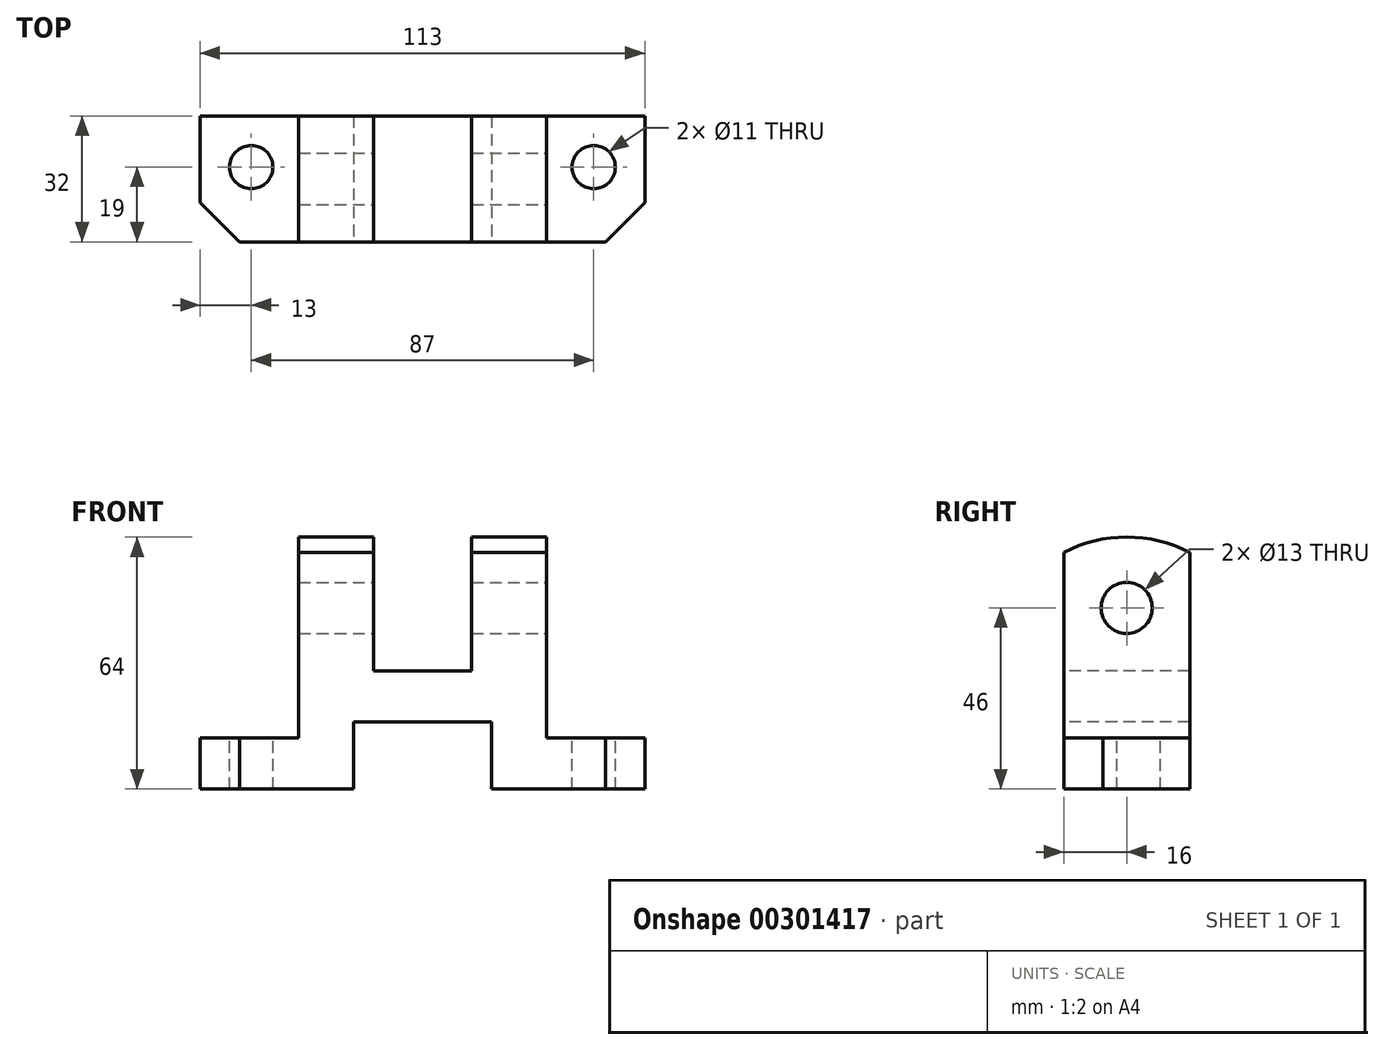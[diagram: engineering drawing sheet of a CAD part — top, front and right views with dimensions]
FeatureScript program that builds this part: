
annotation { "Feature Type Name" : "Feature", "Feature Type Description" : "" }
export const myFeature = defineFeature(function(context is Context, id is Id, definition is map)
    precondition{}
    {
        {
            var Q0;
            Q0=qCreatedBy(makeId("Front.planeOp"),FACE);
            var sketch = newSketch(context, id + "F0", { "sketchPlane" : qUnion([Q0])});
            skLineSegment(sketch, "E0.bottom", {"start": v(-56.5, 64) * mm, "end": v(56.5, 64) * mm});
            skLineSegment(sketch, "E0.top", {"start": v(-56.5, 0) * mm, "end": v(56.5, 0) * mm});
            skLineSegment(sketch, "E0.left", {"start": v(-56.5, 64) * mm, "end": v(-56.5, 0) * mm});
            skLineSegment(sketch, "E0.right", {"start": v(56.5, 64) * mm, "end": v(56.5, 0) * mm});
            skSolve(sketch);
        }
        {
            var Q0;
            Q0=makeQuery(id+"F0.imprint","IMPRINT",FACE,{"disambiguationData":[TD([[makeQuery(id+"F0.imprint","IMPRINT",EDGE,{"derivedFrom":sQuery(id+"F0.wireOp",EDGE,"E0.bottom")}),-1.0]])]});
            extrude(context, id + "F1", {"entities" : qUnion([Q0]), "endBound" : BoundingType.SYMMETRIC, "depth" : 32 * mm});
        }
        {
            var Q0;
            Q0=makeQuery(id+"F1.opExtrude","CAP_FACE",FACE,{"disambiguationData":[OSD([sQuery(id+"F0.wireOp",EDGE,"E0.bottom"),sQuery(id+"F0.wireOp",EDGE,"E0.top"),sQuery(id+"F0.wireOp",EDGE,"E0.left"),sQuery(id+"F0.wireOp",EDGE,"E0.right")])],"isStart":false});
            var sketch = newSketch(context, id + "F2", { "sketchPlane" : qUnion([Q0])});
            skLineSegment(sketch, "E1.bottom", {"start": v(31.5, 64) * mm, "end": v(56.5, 64) * mm});
            skLineSegment(sketch, "E1.top", {"start": v(31.5, 13) * mm, "end": v(56.5, 13) * mm});
            skLineSegment(sketch, "E1.left", {"start": v(31.5, 64) * mm, "end": v(31.5, 13) * mm});
            skLineSegment(sketch, "E1.right", {"start": v(56.5, 64) * mm, "end": v(56.5, 13) * mm});
            skLineSegment(sketch, "E2.bottom", {"start": v(-56.5, 64) * mm, "end": v(-31.5, 64) * mm});
            skLineSegment(sketch, "E2.top", {"start": v(-56.5, 13) * mm, "end": v(-31.5, 13) * mm});
            skLineSegment(sketch, "E2.left", {"start": v(-56.5, 64) * mm, "end": v(-56.5, 13) * mm});
            skLineSegment(sketch, "E2.right", {"start": v(-31.5, 64) * mm, "end": v(-31.5, 13) * mm});
            skLineSegment(sketch, "E3.bottom", {"start": v(-12.5, 64) * mm, "end": v(12.5, 64) * mm});
            skLineSegment(sketch, "E3.top", {"start": v(-12.5, 30) * mm, "end": v(12.5, 30) * mm});
            skLineSegment(sketch, "E3.left", {"start": v(-12.5, 64) * mm, "end": v(-12.5, 30) * mm});
            skLineSegment(sketch, "E3.right", {"start": v(12.5, 64) * mm, "end": v(12.5, 30) * mm});
            skLineSegment(sketch, "E4.bottom", {"start": v(-17.5, 17) * mm, "end": v(17.5, 17) * mm});
            skLineSegment(sketch, "E4.top", {"start": v(-17.5, 0) * mm, "end": v(17.5, 0) * mm});
            skLineSegment(sketch, "E4.left", {"start": v(-17.5, 17) * mm, "end": v(-17.5, 0) * mm});
            skLineSegment(sketch, "E4.right", {"start": v(17.5, 17) * mm, "end": v(17.5, 0) * mm});
            skSolve(sketch);
        }
        {
            var Q0;
            Q0=makeQuery(id+"F2.imprint","IMPRINT",FACE,{"disambiguationData":[TD([[makeQuery(id+"F2.imprint","IMPRINT",EDGE,{"derivedFrom":sQuery(id+"F2.wireOp",EDGE,"E2.bottom")}),-1.0]])]});
            var Q1;
            Q1=makeQuery(id+"F2.imprint","IMPRINT",FACE,{"disambiguationData":[TD([[makeQuery(id+"F2.imprint","IMPRINT",EDGE,{"derivedFrom":sQuery(id+"F2.wireOp",EDGE,"E1.bottom")}),-1.0]])]});
            var Q2;
            Q2=makeQuery(id+"F2.imprint","IMPRINT",FACE,{"disambiguationData":[TD([[makeQuery(id+"F2.imprint","IMPRINT",EDGE,{"derivedFrom":sQuery(id+"F2.wireOp",EDGE,"E3.bottom")}),-1.0]])]});
            var Q3;
            Q3=makeQuery(id+"F2.imprint","IMPRINT",FACE,{"disambiguationData":[TD([[makeQuery(id+"F2.imprint","IMPRINT",EDGE,{"derivedFrom":sQuery(id+"F2.wireOp",EDGE,"E4.bottom")}),-1.0]])]});
            extrude(context, id + "F3", {"entities" : qUnion([Q0, Q1, Q2, Q3]), "operationType" : NewBodyOperationType.REMOVE, "endBound" : BoundingType.THROUGH_ALL, "oppositeDirection" : true, "depth" : 25 * mm});
        }
        {
            var Q0;
            Q0=makeQuery(id+"F3.boolean.opBoolean","COPY",FACE,{"derivedFrom":makeQuery(id+"F3.opExtrude","SWEPT_FACE",FACE,{"disambiguationData":[OSD([sQuery(id+"F2.wireOp",EDGE,"E1.left")])]})});
            var sketch = newSketch(context, id + "F4", { "sketchPlane" : qUnion([Q0])});
            skArc(sketch, "E5", {"start": v(16, 60.13) * mm, "mid": v(0, 64) * mm, "end": v(-16, 60.13) * mm});
            skLineSegment(sketch, "E6", {"start": v(0, 0) * mm, "end": v(0, 85.12) * mm, "construction": true});
            skCircle(sketch, "E7", {"center": v(0, 46) * mm, "radius": 6.5 * mm});
            skSolve(sketch);
        }
        {
            var Q0;
            {var subQ0=sQuery(id+"F4.wireOp",EDGE,"E5");var subQ1=sQuery(id+"F2.wireOp",EDGE,"E1.left");var subQ2=makeQuery(id+"F3.boolean.opBoolean","COPY",EDGE,{"derivedFrom":makeQuery(id+"F3.opExtrude","CAP_EDGE",EDGE,{"disambiguationData":[OSD([subQ1])],"isStart":true})});var subQ3=makeQuery(id+"F4.imprint","INTERSECT",VERTEX,{"derivedFrom":[subQ2,subQ0]});Q0=makeQuery(id+"F4.imprint","IMPRINT",FACE,{"disambiguationData":[TD([[makeQuery(id+"F4.imprint","IMPRINT",EDGE,{"disambiguationData":[TD([[subQ3,1.0]])],"derivedFrom":subQ0}),-1.0]])]});}
            var Q1;
            {var subQ0=sQuery(id+"F4.wireOp",EDGE,"E5");var subQ1=sQuery(id+"F2.wireOp",EDGE,"E1.left");var subQ2=sQuery(id+"F0.wireOp",EDGE,"E0.bottom");var subQ5=makeQuery(id+"F3.boolean.opBoolean","COPY",EDGE,{"derivedFrom":makeQuery(id+"F3.opExtrude","SWEPT_EDGE",EDGE,{"disambiguationData":[OSD([subQ2,sQuery(id+"F2.wireOp",EDGE,"E1.bottom"),subQ1])]})});var subQ6=makeQuery(id+"F4.imprint","INTERSECT",VERTEX,{"derivedFrom":[subQ5,subQ0]});Q1=makeQuery(id+"F4.imprint","IMPRINT",FACE,{"disambiguationData":[TD([[makeQuery(id+"F4.imprint","IMPRINT",EDGE,{"disambiguationData":[TD([[subQ6,1.0]])],"derivedFrom":subQ0}),-1.0]])]});}
            var Q2;
            Q2=makeQuery(id+"F4.imprint","IMPRINT",FACE,{"disambiguationData":[TD([[makeQuery(id+"F4.imprint","IMPRINT",EDGE,{"derivedFrom":sQuery(id+"F4.wireOp",EDGE,"E7")}),1.0]])]});
            extrude(context, id + "F5", {"entities" : qUnion([Q0, Q1, Q2]), "operationType" : NewBodyOperationType.REMOVE, "endBound" : BoundingType.THROUGH_ALL, "oppositeDirection" : true, "depth" : 25 * mm});
        }
        {
            var Q0;
            Q0=qCreatedBy(makeId("Top.planeOp"),FACE);
            cPlane(context, id + "F6", {"entities" : qUnion([Q0]), "cplaneType" : CPlaneType.OFFSET, "offset" : 64 * mm, "width" : 150 * mm, "height" : 150 * mm});
        }
        {
            var Q0;
            Q0=qCreatedBy(id+"F6.planeOp",FACE);
            var sketch = newSketch(context, id + "F7", { "sketchPlane" : qUnion([Q0])});
            skCircle(sketch, "E8", {"center": v(43.5, 3) * mm, "radius": 5.5 * mm});
            skCircle(sketch, "E9", {"center": v(-43.5, 3) * mm, "radius": 5.5 * mm});
            skSolve(sketch);
        }
        {
            var Q0;
            Q0=makeQuery(id+"F7.imprint","IMPRINT",FACE,{"disambiguationData":[TD([[makeQuery(id+"F7.imprint","IMPRINT",EDGE,{"derivedFrom":sQuery(id+"F7.wireOp",EDGE,"E9")}),1.0]])]});
            var Q1;
            Q1=makeQuery(id+"F7.imprint","IMPRINT",FACE,{"disambiguationData":[TD([[makeQuery(id+"F7.imprint","IMPRINT",EDGE,{"derivedFrom":sQuery(id+"F7.wireOp",EDGE,"E8")}),1.0]])]});
            extrude(context, id + "F8", {"entities" : qUnion([Q0, Q1]), "operationType" : NewBodyOperationType.REMOVE, "endBound" : BoundingType.THROUGH_ALL, "oppositeDirection" : true, "depth" : 25 * mm});
        }
        {
            var Q0;
            Q0=makeQuery(id+"F1.opExtrude","CAP_EDGE",EDGE,{"disambiguationData":[OSD([sQuery(id+"F0.wireOp",EDGE,"E0.right")])],"isStart":false});
            var Q1;
            Q1=makeQuery(id+"F1.opExtrude","CAP_EDGE",EDGE,{"disambiguationData":[OSD([sQuery(id+"F0.wireOp",EDGE,"E0.left")])],"isStart":false});
            chamfer(context, id + "F9", {"entities" : qUnion([Q0, Q1]), "width" : 10 * mm, "tangentPropagation" : true});
        }
    });
